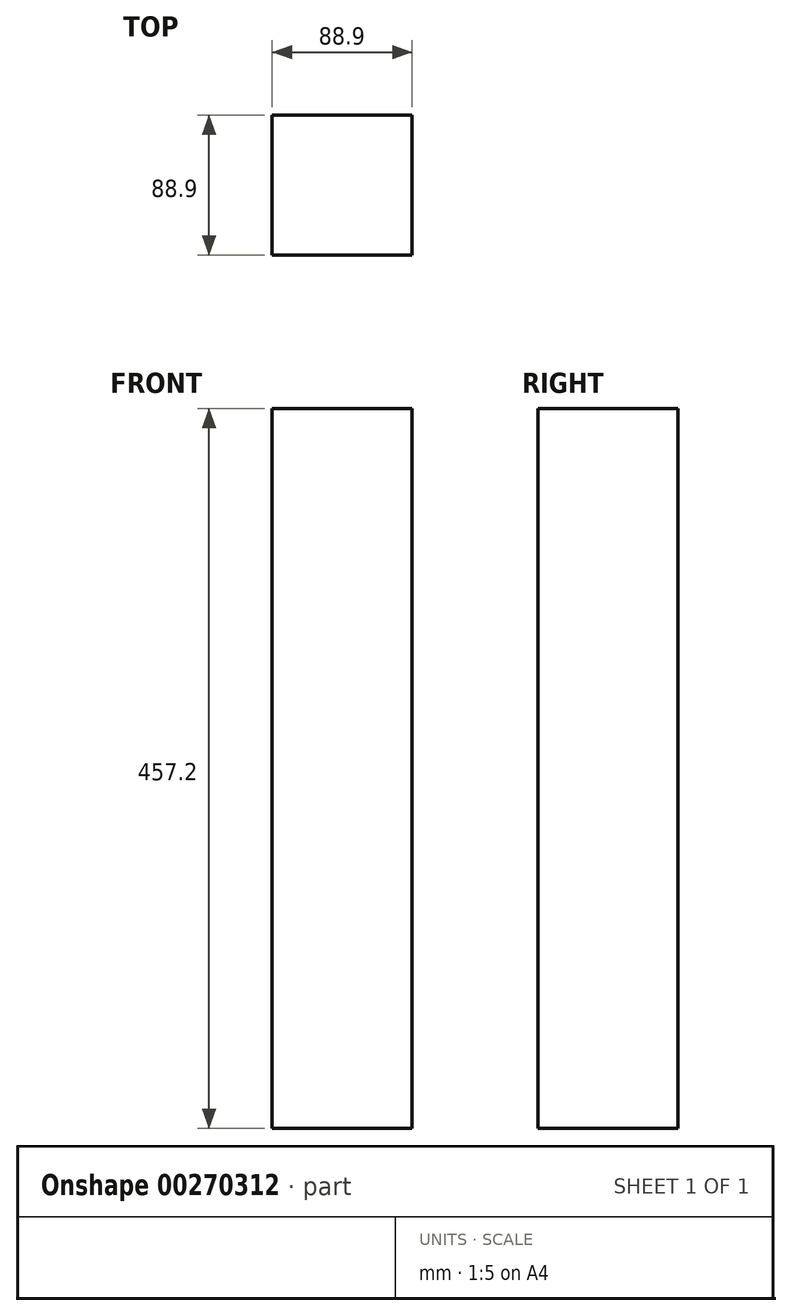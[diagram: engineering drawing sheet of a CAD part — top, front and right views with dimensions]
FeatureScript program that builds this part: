
annotation { "Feature Type Name" : "Feature", "Feature Type Description" : "" }
export const myFeature = defineFeature(function(context is Context, id is Id, definition is map)
    precondition{}
    {
        {
            var Q0;
            Q0=qCreatedBy(makeId("Top.planeOp"),FACE);
            var sketch = newSketch(context, id + "F0", { "sketchPlane" : qUnion([Q0])});
            skLineSegment(sketch, "E0.bottom", {"start": v(44.45, -44.45) * mm, "end": v(-44.45, -44.45) * mm});
            skLineSegment(sketch, "E0.top", {"start": v(44.45, 44.45) * mm, "end": v(-44.45, 44.45) * mm});
            skLineSegment(sketch, "E0.left", {"start": v(44.45, -44.45) * mm, "end": v(44.45, 44.45) * mm});
            skLineSegment(sketch, "E0.right", {"start": v(-44.45, -44.45) * mm, "end": v(-44.45, 44.45) * mm});
            skPoint(sketch, "E0.middle", {"position": v(0, 0) * mm});
            skSolve(sketch);
        }
        {
            var Q0;
            Q0=makeQuery(id+"F0.imprint","IMPRINT",FACE,{"disambiguationData":[TD([[makeQuery(id+"F0.imprint","IMPRINT",EDGE,{"derivedFrom":sQuery(id+"F0.wireOp",EDGE,"E0.bottom")}),-1.0]])]});
            extrude(context, id + "F1", {"entities" : qUnion([Q0]), "endBound" : BoundingType.SYMMETRIC, "depth" : 457.2 * mm});
        }
    });
